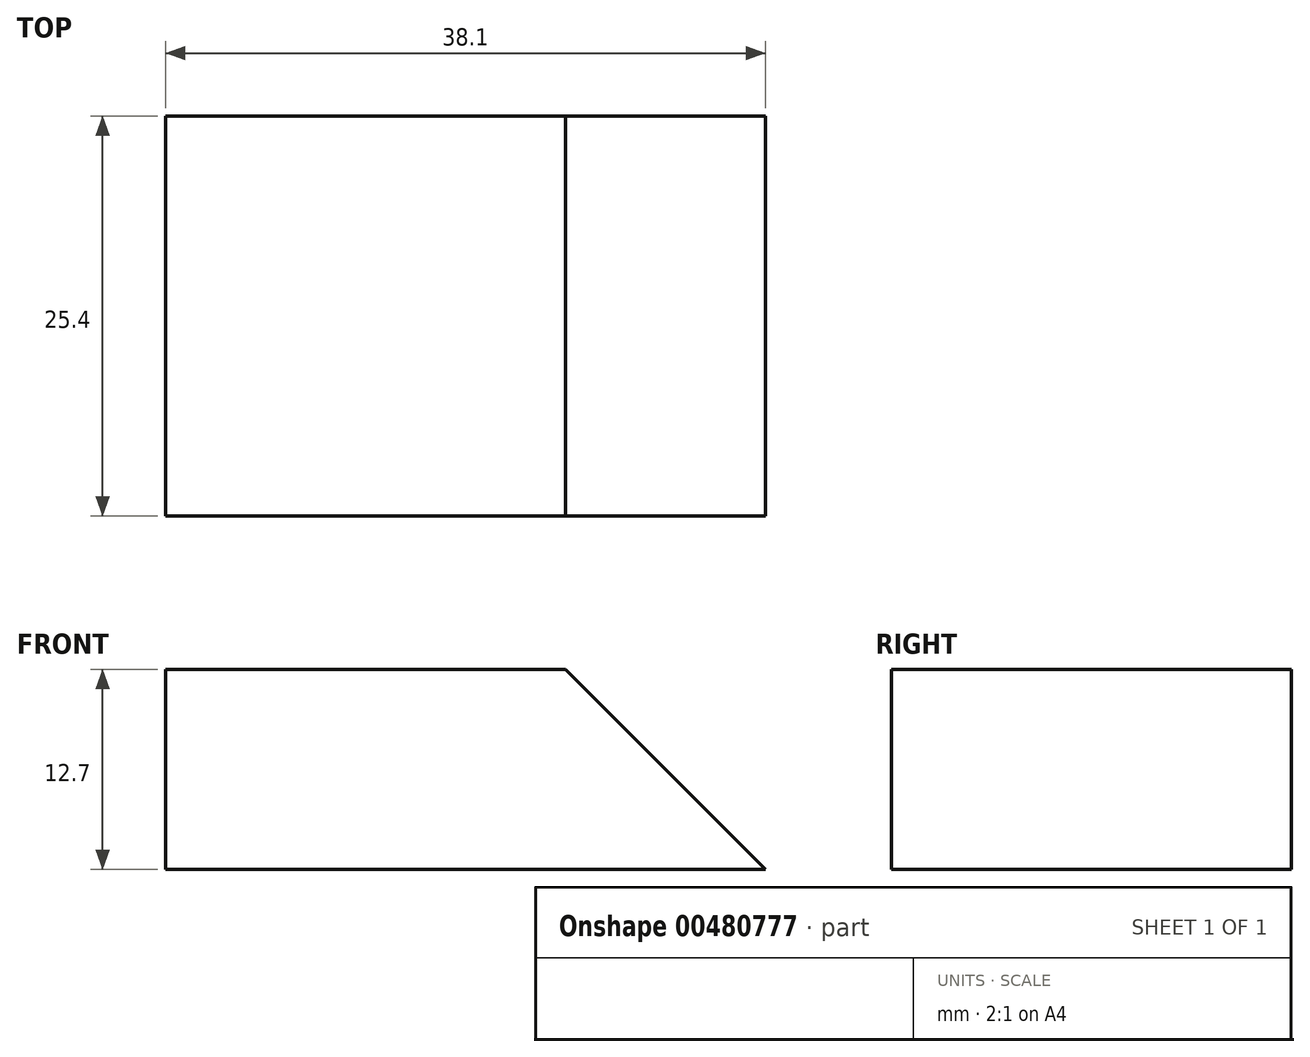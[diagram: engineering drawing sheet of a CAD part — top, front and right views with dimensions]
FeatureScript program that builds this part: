
annotation { "Feature Type Name" : "Feature", "Feature Type Description" : "" }
export const myFeature = defineFeature(function(context is Context, id is Id, definition is map)
    precondition{}
    {
        {
            var Q0;
            Q0=qCreatedBy(makeId("Front.planeOp"),FACE);
            var sketch = newSketch(context, id + "F0", { "sketchPlane" : qUnion([Q0])});
            skLineSegment(sketch, "E0", {"start": v(0, 0) * mm, "end": v(38.1, 0) * mm});
            skLineSegment(sketch, "E1", {"start": v(0, 0) * mm, "end": v(0, 12.7) * mm});
            skLineSegment(sketch, "E2", {"start": v(0, 12.7) * mm, "end": v(25.4, 12.7) * mm});
            skLineSegment(sketch, "E3", {"start": v(25.4, 12.7) * mm, "end": v(38.1, 0) * mm});
            skSolve(sketch);
        }
        {
            var Q0;
            Q0 = qSketchRegion(id + "F0", true);
            extrude(context, id + "F1", {"entities" : qUnion([Q0]), "depth" : 25.4 * mm});
        }
    });
